# Revit family: Supports-Teknion-CEWIS-Island_Structure_Gables_Storage_One_Side-Expansion_Casework+-R2023
name_source: partatom
category: Furniture
units: mm (PartAtom-declared; Revit-internal decimal feet)

## family parameters
Always vertical = Yes
Cut with Voids When Loaded = No
Enable Cutting in Views = No
OmniClass Number = 23.40.20.00
OmniClass Title = General Furniture and Specialties
Render Appearance Source = Family Geometry
Room Calculation Point = No
Shared = Yes
Work Plane-Based = No

## types (2) — shared parameters
Assembly Code = E2020200
Description = Island Structure with Gables – Storage on One Side
Manufacturer = Teknion
Manufacturer Fax = 416.661.4586
Model = CEWIS
Product Documentation Link = https://www.teknion.com
Product Line = Countertop & Supports
Product Page URL = https://www.teknion.com
Series = Expansion Casework +
Sustainability Data = https://www.teknion.com
URL = www.teknion.com
Unit Weight URL = http://www.teknion.com
Warranty = http://www.teknion.com
zero-valued in all types: Default Elevation

## per-type parameters (varying)
| type | F | Part Number | R |
| (F) Flush Front | Yes | CEWIS_________F | No |
| (R) Recessed Front | No | CEWIS_________R | Yes |

## geometry (parser evidence)
native form markers: Sweep x3
no freeform markers — native parametric forms only
